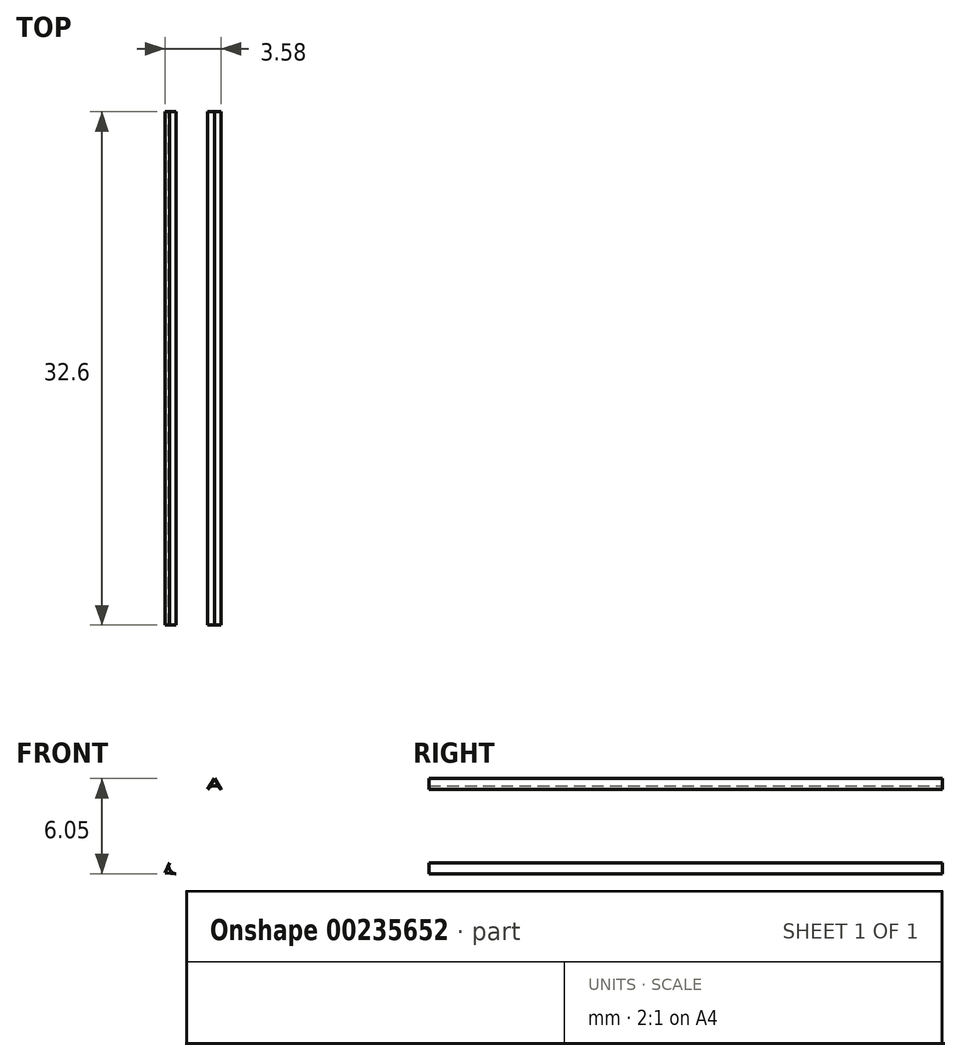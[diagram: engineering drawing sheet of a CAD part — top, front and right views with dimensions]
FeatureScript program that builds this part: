
annotation { "Feature Type Name" : "Feature", "Feature Type Description" : "" }
export const myFeature = defineFeature(function(context is Context, id is Id, definition is map)
    precondition{}
    {
        {
            var Q0;
            Q0=qCreatedBy(makeId("Front.planeOp"),FACE);
            var sketch = newSketch(context, id + "F0", { "sketchPlane" : qUnion([Q0])});
            skFitSpline(sketch, "E0", {"points": [v(0, 0) * mm, v(1.44, 3.07) * mm, v(3.15, 6) * mm], "startDerivative": vector(2.75, 6.2) * mm, "endDerivative": vector(3.55, 5.8) * mm});
            skFitSpline(sketch, "E1", {"points": [v(3.15, 6) * mm, v(4.86, 3.07) * mm, v(6.3, 0) * mm], "startDerivative": vector(3.55, -5.8) * mm, "endDerivative": vector(2.75, -6.2) * mm});
            skFitSpline(sketch, "E2", {"points": [v(6.3, 0) * mm, v(3.15, -0.15) * mm, v(0, 0) * mm], "startDerivative": vector(-6.3, -0.45) * mm, "endDerivative": vector(-6.3, 0.45) * mm});
            skArc(sketch, "E3.filletArc", {"start": v(3.58, 5.3) * mm, "mid": v(3.15, 5.54) * mm, "end": v(2.72, 5.3) * mm});
            skArc(sketch, "E4.filletArc", {"start": v(5.59, -0.05) * mm, "mid": v(5.98, 0.2) * mm, "end": v(6, 0.65) * mm});
            skArc(sketch, "E5.filletArc", {"start": v(0.3, 0.65) * mm, "mid": v(0.32, 0.2) * mm, "end": v(0.71, -0.05) * mm});
            skSolve(sketch);
        }
        {
            var Q0;
            Q0=makeQuery(id+"F0.imprint","IMPRINT",FACE,{"disambiguationData":[TD([[makeQuery(id+"F0.imprint","IMPRINT",EDGE,{"derivedFrom":sQuery(id+"F0.wireOp",EDGE,"E0")}),-1.0]])]});
            extrude(context, id + "F1", {"entities" : qUnion([Q0]), "depth" : 32.6 * mm});
        }
    });
